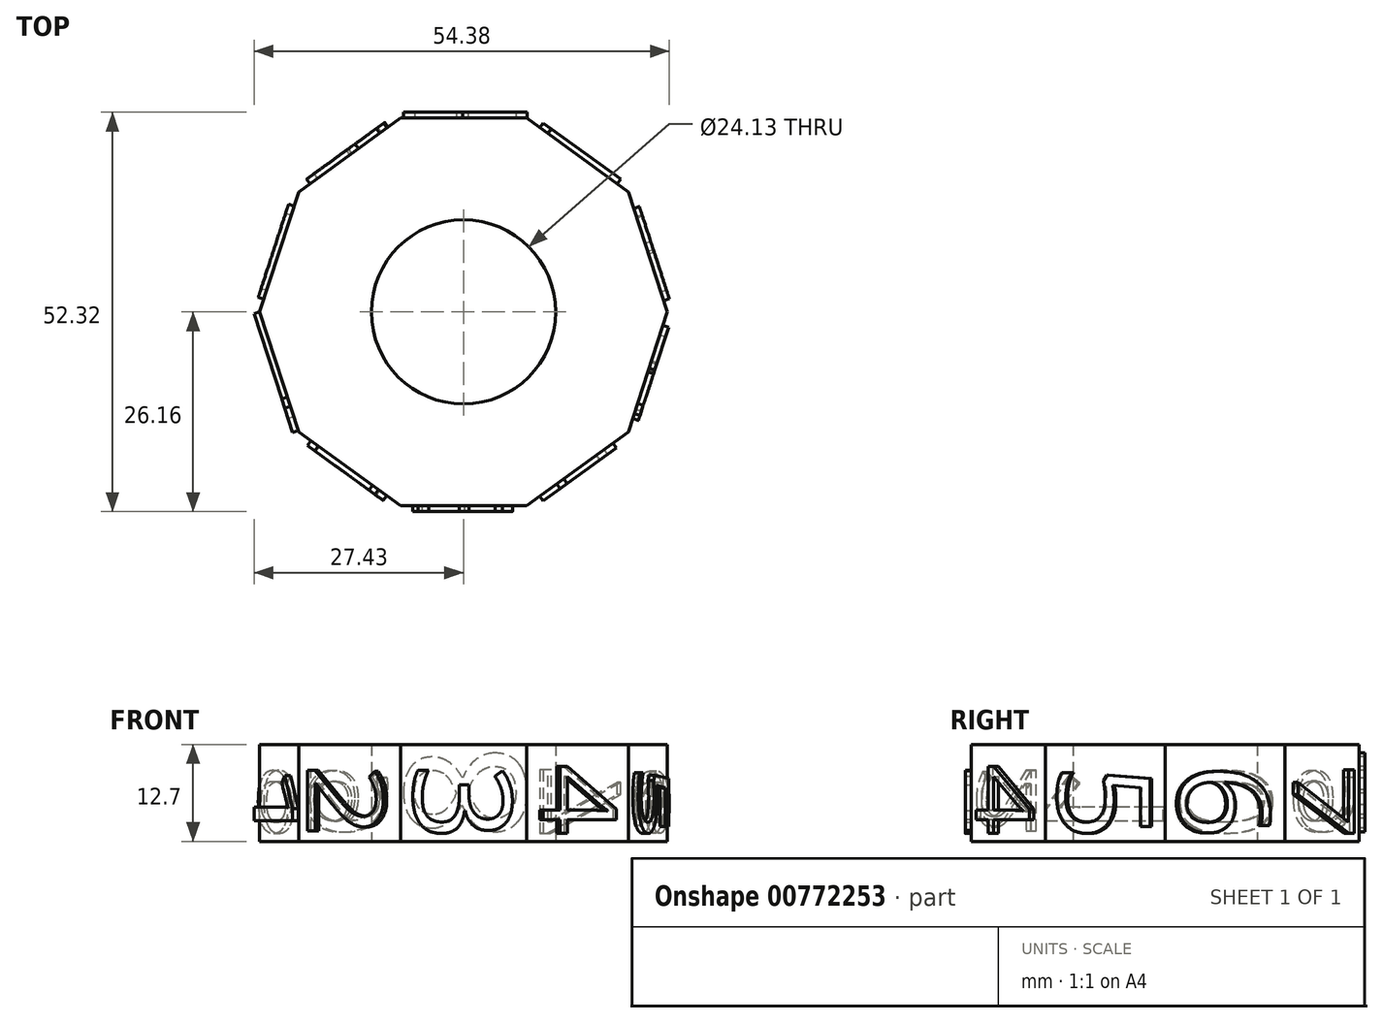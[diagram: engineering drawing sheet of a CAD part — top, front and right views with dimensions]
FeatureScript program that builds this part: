
annotation { "Feature Type Name" : "Feature", "Feature Type Description" : "" }
export const myFeature = defineFeature(function(context is Context, id is Id, definition is map)
    precondition{}
    {
        {
            var Q0;
            Q0=qCreatedBy(makeId("Top.planeOp"),FACE);
            var sketch = newSketch(context, id + "F0", { "sketchPlane" : qUnion([Q0])});
            skCircle(sketch, "E0", {"center": v(0, 0) * mm, "radius": 12.07 * mm});
            skCircle(sketch, "E1.cCircle", {"center": v(0, 0) * mm, "radius": 25.4 * mm, "construction": true});
            skLineSegment(sketch, "E1.0", {"start": v(-8.25, 25.4) * mm, "end": v(8.25, 25.4) * mm});
            skLineSegment(sketch, "E1.1", {"start": v(8.25, 25.4) * mm, "end": v(21.6, 15.7) * mm});
            skLineSegment(sketch, "E1.2", {"start": v(21.6, 15.7) * mm, "end": v(26.7, 0) * mm});
            skLineSegment(sketch, "E1.3", {"start": v(26.7, 0) * mm, "end": v(21.6, -15.7) * mm});
            skLineSegment(sketch, "E1.4", {"start": v(21.6, -15.7) * mm, "end": v(8.25, -25.4) * mm});
            skLineSegment(sketch, "E1.5", {"start": v(8.25, -25.4) * mm, "end": v(-8.25, -25.4) * mm});
            skLineSegment(sketch, "E1.6", {"start": v(-8.25, -25.4) * mm, "end": v(-21.6, -15.7) * mm});
            skLineSegment(sketch, "E1.7", {"start": v(-21.6, -15.7) * mm, "end": v(-26.7, 0) * mm});
            skLineSegment(sketch, "E1.8", {"start": v(-26.7, 0) * mm, "end": v(-21.6, 15.7) * mm});
            skLineSegment(sketch, "E1.9", {"start": v(-21.6, 15.7) * mm, "end": v(-8.25, 25.4) * mm});
            skPoint(sketch, "E1.0.midPoint", {"position": v(0, 25.4) * mm});
            skSolve(sketch);
        }
        {
            var Q0;
            Q0 = qSketchRegion(id + "F0", true);
            extrude(context, id + "F1", {"entities" : qUnion([Q0]), "depth" : 12.7 * mm, "offsetDistance" : 25.4 * mm});
        }
        {
            var Q0;
            Q0=makeQuery(id+"F1.opExtrude","SWEPT_FACE",FACE,{"disambiguationData":[OSD([sQuery(id+"F0.wireOp",EDGE,"E1.7")])]});
            var sketch = newSketch(context, id + "F2", { "sketchPlane" : qUnion([Q0])});
            skText(sketch, "E2", { "text": "1", "fontName": "OpenSans-Regular.ttf"});
            const initialGuessF2  = {"E2": [-0.00825, 0.0107, 0, -1, 0.0165]};
            skSetInitialGuess(sketch, initialGuessF2);
            skSolve(sketch);
        }
        {
            var Q0;
            Q0 = qSketchRegion(id + "F2", true);
            extrude(context, id + "F3", {"entities" : qUnion([Q0]), "operationType" : NewBodyOperationType.ADD, "depth" : 0.76 * mm, "offsetDistance" : 25.4 * mm});
        }
        {
            var Q0;
            Q0=makeQuery(id+"F1.opExtrude","SWEPT_FACE",FACE,{"disambiguationData":[OSD([sQuery(id+"F0.wireOp",EDGE,"E1.6")])]});
            var sketch = newSketch(context, id + "F4", { "sketchPlane" : qUnion([Q0])});
            skText(sketch, "E3", { "text": "2", "fontName": "OpenSans-Regular.ttf"});
            const initialGuessF4  = {"E3": [-0.00624, 0.01016, 0, -1, 0.0122]};
            skSetInitialGuess(sketch, initialGuessF4);
            skSolve(sketch);
        }
        {
            var Q0;
            Q0 = qSketchRegion(id + "F4", true);
            extrude(context, id + "F5", {"entities" : qUnion([Q0]), "operationType" : NewBodyOperationType.ADD, "depth" : 0.76 * mm, "offsetDistance" : 25.4 * mm});
        }
        {
            var Q0;
            Q0=makeQuery(id+"F1.opExtrude","SWEPT_FACE",FACE,{"disambiguationData":[OSD([sQuery(id+"F0.wireOp",EDGE,"E1.5")])]});
            var sketch = newSketch(context, id + "F6", { "sketchPlane" : qUnion([Q0])});
            skText(sketch, "E4", { "text": "3", "fontName": "OpenSans-Regular.ttf"});
            const initialGuessF6  = {"E4": [-0.00647, 0.01016, 0, -1, 0.0128]};
            skSetInitialGuess(sketch, initialGuessF6);
            skSolve(sketch);
        }
        {
            var Q0;
            Q0 = qSketchRegion(id + "F6", true);
            extrude(context, id + "F7", {"entities" : qUnion([Q0]), "operationType" : NewBodyOperationType.ADD, "depth" : 0.76 * mm, "offsetDistance" : 25.4 * mm});
        }
        {
            var Q0;
            Q0=makeQuery(id+"F1.opExtrude","SWEPT_FACE",FACE,{"disambiguationData":[OSD([sQuery(id+"F0.wireOp",EDGE,"E1.4")])]});
            var sketch = newSketch(context, id + "F8", { "sketchPlane" : qUnion([Q0])});
            skText(sketch, "E5", { "text": "4", "fontName": "OpenSans-Regular.ttf"});
            const initialGuessF8  = {"E5": [-0.00611, 0.01016, 0, -1, 0.01188]};
            skSetInitialGuess(sketch, initialGuessF8);
            skSolve(sketch);
        }
        {
            var Q0;
            Q0 = qSketchRegion(id + "F8", true);
            extrude(context, id + "F9", {"entities" : qUnion([Q0]), "operationType" : NewBodyOperationType.ADD, "depth" : 0.76 * mm, "offsetDistance" : 25.4 * mm});
        }
        {
            var Q0;
            Q0=makeQuery(id+"F1.opExtrude","SWEPT_FACE",FACE,{"disambiguationData":[OSD([sQuery(id+"F0.wireOp",EDGE,"E1.3")])]});
            var sketch = newSketch(context, id + "F10", { "sketchPlane" : qUnion([Q0])});
            skText(sketch, "E6", { "text": "5", "fontName": "OpenSans-Regular.ttf"});
            const initialGuessF10  = {"E6": [-0.00625, 0.01016, 0, -1, 0.01276]};
            skSetInitialGuess(sketch, initialGuessF10);
            skSolve(sketch);
        }
        {
            var Q0;
            Q0 = qSketchRegion(id + "F10", true);
            extrude(context, id + "F11", {"entities" : qUnion([Q0]), "operationType" : NewBodyOperationType.ADD, "depth" : 0.76 * mm, "offsetDistance" : 25.4 * mm});
        }
        {
            var Q0;
            Q0=makeQuery(id+"F1.opExtrude","SWEPT_FACE",FACE,{"disambiguationData":[OSD([sQuery(id+"F0.wireOp",EDGE,"E1.2")])]});
            var sketch = newSketch(context, id + "F12", { "sketchPlane" : qUnion([Q0])});
            skText(sketch, "E7", { "text": "6", "fontName": "OpenSans-Regular.ttf"});
            const initialGuessF12  = {"E7": [-0.00653, 0.01016, 0, -1, 0.01248]};
            skSetInitialGuess(sketch, initialGuessF12);
            skSolve(sketch);
        }
        {
            var Q0;
            Q0 = qSketchRegion(id + "F12", true);
            extrude(context, id + "F13", {"entities" : qUnion([Q0]), "operationType" : NewBodyOperationType.ADD, "depth" : 0.76 * mm, "offsetDistance" : 25.4 * mm});
        }
        {
            var Q0;
            Q0=makeQuery(id+"F1.opExtrude","SWEPT_FACE",FACE,{"disambiguationData":[OSD([sQuery(id+"F0.wireOp",EDGE,"E1.1")])]});
            var sketch = newSketch(context, id + "F14", { "sketchPlane" : qUnion([Q0])});
            skText(sketch, "E8", { "text": "7", "fontName": "OpenSans-Regular.ttf"});
            const initialGuessF14  = {"E8": [-0.00641, 0.01016, 0, -1, 0.01261]};
            skSetInitialGuess(sketch, initialGuessF14);
            skSolve(sketch);
        }
        {
            var Q0;
            Q0 = qSketchRegion(id + "F14", true);
            extrude(context, id + "F15", {"entities" : qUnion([Q0]), "operationType" : NewBodyOperationType.ADD, "depth" : 0.76 * mm, "offsetDistance" : 25.4 * mm});
        }
        {
            var Q0;
            Q0=makeQuery(id+"F1.opExtrude","SWEPT_FACE",FACE,{"disambiguationData":[OSD([sQuery(id+"F0.wireOp",EDGE,"E1.0")])]});
            var sketch = newSketch(context, id + "F16", { "sketchPlane" : qUnion([Q0])});
            skText(sketch, "E9", { "text": "8", "fontName": "OpenSans-Regular.ttf"});
            const initialGuessF16  = {"E9": [-0.00808, 0.0127, 0, -1, 0.01586]};
            skSetInitialGuess(sketch, initialGuessF16);
            skSolve(sketch);
        }
        {
            var Q0;
            Q0 = qSketchRegion(id + "F16", true);
            extrude(context, id + "F17", {"entities" : qUnion([Q0]), "operationType" : NewBodyOperationType.ADD, "depth" : 0.76 * mm, "offsetDistance" : 25.4 * mm});
        }
        {
            var Q0;
            Q0=makeQuery(id+"F1.opExtrude","SWEPT_FACE",FACE,{"disambiguationData":[OSD([sQuery(id+"F0.wireOp",EDGE,"E1.9")])]});
            var sketch = newSketch(context, id + "F18", { "sketchPlane" : qUnion([Q0])});
            skText(sketch, "E10", { "text": "9", "fontName": "OpenSans-Regular.ttf"});
            const initialGuessF18  = {"E10": [-0.00607, 0.01016, 0, -1, 0.0124]};
            skSetInitialGuess(sketch, initialGuessF18);
            skSolve(sketch);
        }
        {
            var Q0;
            Q0 = qSketchRegion(id + "F18", true);
            extrude(context, id + "F19", {"entities" : qUnion([Q0]), "operationType" : NewBodyOperationType.ADD, "depth" : 0.76 * mm, "offsetDistance" : 25.4 * mm});
        }
        {
            var Q0;
            Q0=makeQuery(id+"F1.opExtrude","SWEPT_FACE",FACE,{"disambiguationData":[OSD([sQuery(id+"F0.wireOp",EDGE,"E1.8")])]});
            var sketch = newSketch(context, id + "F20", { "sketchPlane" : qUnion([Q0])});
            skText(sketch, "E11", { "text": "0", "fontName": "OpenSans-Regular.ttf"});
            const initialGuessF20  = {"E11": [-0.00615, 0.01016, 0, -1, 0.01253]};
            skSetInitialGuess(sketch, initialGuessF20);
            skSolve(sketch);
        }
        {
            var Q0;
            Q0 = qSketchRegion(id + "F20", true);
            extrude(context, id + "F21", {"entities" : qUnion([Q0]), "operationType" : NewBodyOperationType.ADD, "depth" : 0.76 * mm, "offsetDistance" : 25.4 * mm});
        }
    });
